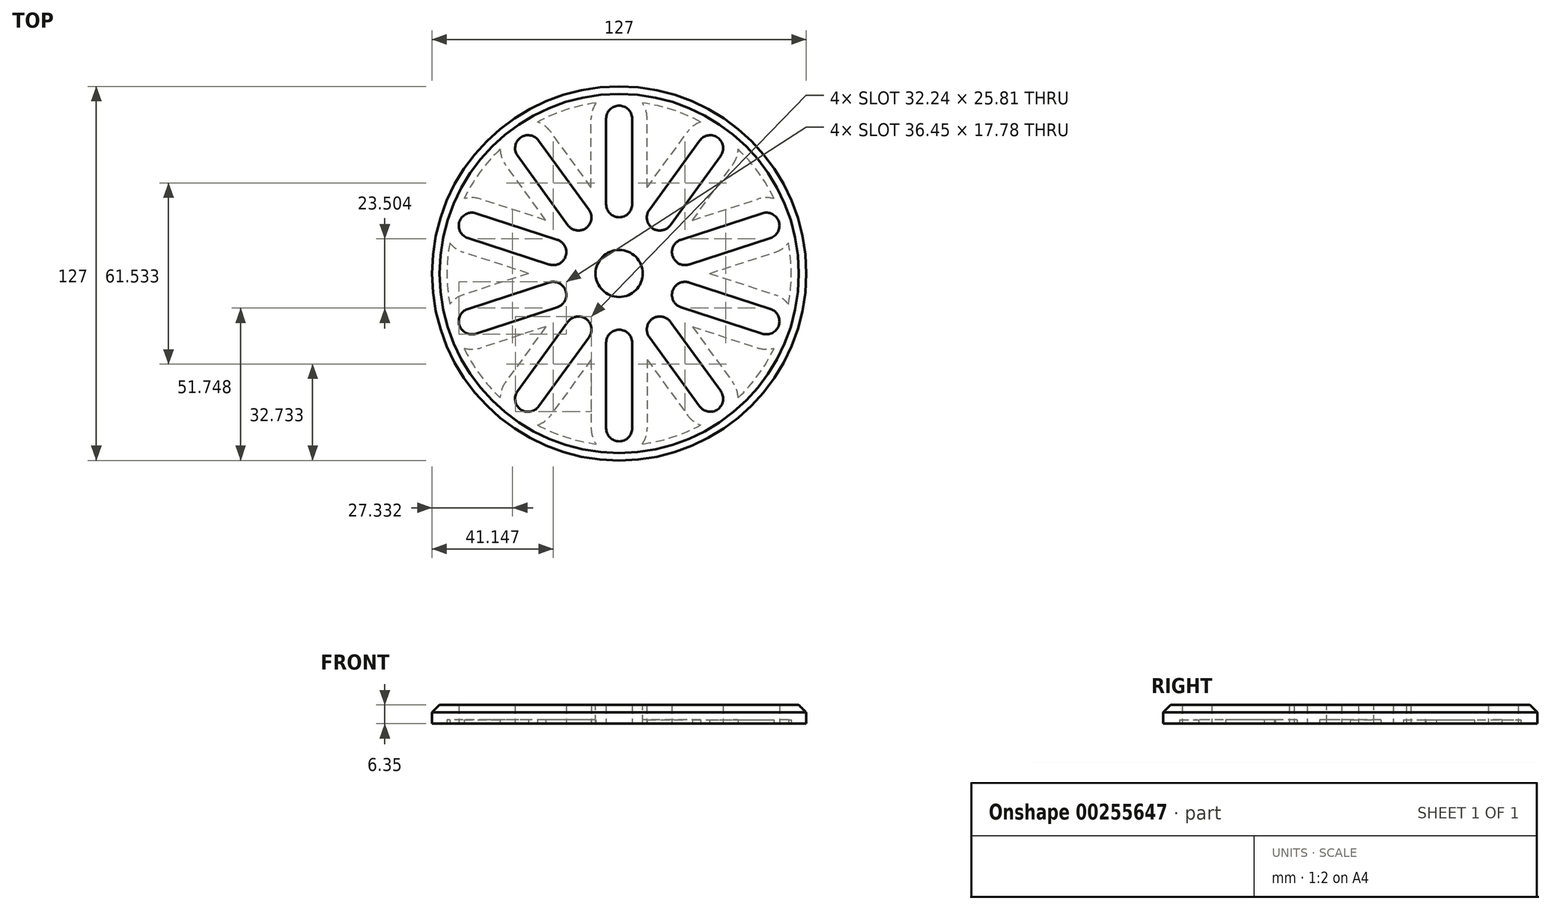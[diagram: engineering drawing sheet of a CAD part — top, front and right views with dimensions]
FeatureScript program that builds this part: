
annotation { "Feature Type Name" : "Feature", "Feature Type Description" : "" }
export const myFeature = defineFeature(function(context is Context, id is Id, definition is map)
    precondition{}
    {
        {
            var Q0;
            Q0=qCreatedBy(makeId("Top.planeOp"),FACE);
            var sketch = newSketch(context, id + "F0", { "sketchPlane" : qUnion([Q0])});
            skCircle(sketch, "E0", {"center": v(0, 0) * mm, "radius": 63.5 * mm});
            skCircle(sketch, "E1", {"center": v(0, 0) * mm, "radius": 12.7 * mm});
            skLineSegment(sketch, "E2.left", {"start": v(4.41, 23.5) * mm, "end": v(4.41, 52.57) * mm});
            skLineSegment(sketch, "E2.right", {"start": v(-4.41, 23.5) * mm, "end": v(-4.41, 52.57) * mm});
            skPoint(sketch, "E2.middle", {"position": v(0, 38.03) * mm});
            skArc(sketch, "E3", {"start": v(-4.41, 23.5) * mm, "mid": v(0, 19.08) * mm, "end": v(4.41, 23.5) * mm});
            skArc(sketch, "E4", {"start": v(4.41, 52.57) * mm, "mid": v(0, 56.98) * mm, "end": v(-4.41, 52.57) * mm});
            skPoint(sketch, "E5.1.0", {"position": v(-22.35, 30.77) * mm});
            skArc(sketch, "E5.1.1", {"start": v(-27.33, 45.12) * mm, "mid": v(-33.5, 46.1) * mm, "end": v(-34.47, 39.94) * mm});
            skArc(sketch, "E5.1.2", {"start": v(-17.38, 16.41) * mm, "mid": v(-11.21, 15.43) * mm, "end": v(-10.24, 21.6) * mm});
            skLineSegment(sketch, "E5.1.3", {"start": v(-17.38, 16.41) * mm, "end": v(-34.47, 39.94) * mm});
            skLineSegment(sketch, "E5.1.4", {"start": v(-10.24, 21.6) * mm, "end": v(-27.33, 45.12) * mm});
            skPoint(sketch, "E5.2.0", {"position": v(-36.17, 11.75) * mm});
            skArc(sketch, "E5.2.1", {"start": v(-48.63, 20.44) * mm, "mid": v(-54.2, 17.6) * mm, "end": v(-51.36, 12.05) * mm});
            skArc(sketch, "E5.2.2", {"start": v(-23.7, 3.06) * mm, "mid": v(-18.14, 5.9) * mm, "end": v(-20.98, 11.46) * mm});
            skLineSegment(sketch, "E5.2.3", {"start": v(-23.7, 3.06) * mm, "end": v(-51.36, 12.05) * mm});
            skLineSegment(sketch, "E5.2.4", {"start": v(-20.98, 11.46) * mm, "end": v(-48.63, 20.44) * mm});
            skPoint(sketch, "E5.3.0", {"position": v(-36.17, -11.75) * mm});
            skArc(sketch, "E5.3.1", {"start": v(-51.36, -12.05) * mm, "mid": v(-54.2, -17.6) * mm, "end": v(-48.63, -20.44) * mm});
            skArc(sketch, "E5.3.2", {"start": v(-20.98, -11.46) * mm, "mid": v(-18.14, -5.9) * mm, "end": v(-23.7, -3.06) * mm});
            skLineSegment(sketch, "E5.3.3", {"start": v(-20.98, -11.46) * mm, "end": v(-48.63, -20.44) * mm});
            skLineSegment(sketch, "E5.3.4", {"start": v(-23.7, -3.06) * mm, "end": v(-51.36, -12.05) * mm});
            skPoint(sketch, "E5.4.0", {"position": v(-22.35, -30.77) * mm});
            skArc(sketch, "E5.4.1", {"start": v(-34.47, -39.94) * mm, "mid": v(-33.5, -46.1) * mm, "end": v(-27.33, -45.12) * mm});
            skArc(sketch, "E5.4.2", {"start": v(-10.24, -21.6) * mm, "mid": v(-11.21, -15.43) * mm, "end": v(-17.38, -16.41) * mm});
            skLineSegment(sketch, "E5.4.3", {"start": v(-10.24, -21.6) * mm, "end": v(-27.33, -45.12) * mm});
            skLineSegment(sketch, "E5.4.4", {"start": v(-17.38, -16.41) * mm, "end": v(-34.47, -39.94) * mm});
            skPoint(sketch, "E5.5.0", {"position": v(0, -38.03) * mm});
            skArc(sketch, "E5.5.1", {"start": v(-4.41, -52.57) * mm, "mid": v(0, -56.98) * mm, "end": v(4.41, -52.57) * mm});
            skArc(sketch, "E5.5.2", {"start": v(4.41, -23.5) * mm, "mid": v(0, -19.08) * mm, "end": v(-4.41, -23.5) * mm});
            skLineSegment(sketch, "E5.5.3", {"start": v(4.41, -23.5) * mm, "end": v(4.41, -52.57) * mm});
            skLineSegment(sketch, "E5.5.4", {"start": v(-4.41, -23.5) * mm, "end": v(-4.41, -52.57) * mm});
            skPoint(sketch, "E5.6.0", {"position": v(22.35, -30.77) * mm});
            skArc(sketch, "E5.6.1", {"start": v(27.33, -45.12) * mm, "mid": v(33.5, -46.1) * mm, "end": v(34.47, -39.94) * mm});
            skArc(sketch, "E5.6.2", {"start": v(17.38, -16.41) * mm, "mid": v(11.21, -15.43) * mm, "end": v(10.24, -21.6) * mm});
            skLineSegment(sketch, "E5.6.3", {"start": v(17.38, -16.41) * mm, "end": v(34.47, -39.94) * mm});
            skLineSegment(sketch, "E5.6.4", {"start": v(10.24, -21.6) * mm, "end": v(27.33, -45.12) * mm});
            skPoint(sketch, "E5.7.0", {"position": v(36.17, -11.75) * mm});
            skArc(sketch, "E5.7.1", {"start": v(48.63, -20.44) * mm, "mid": v(54.2, -17.6) * mm, "end": v(51.36, -12.05) * mm});
            skArc(sketch, "E5.7.2", {"start": v(23.7, -3.06) * mm, "mid": v(18.14, -5.9) * mm, "end": v(20.98, -11.46) * mm});
            skLineSegment(sketch, "E5.7.3", {"start": v(23.7, -3.06) * mm, "end": v(51.36, -12.05) * mm});
            skLineSegment(sketch, "E5.7.4", {"start": v(20.98, -11.46) * mm, "end": v(48.63, -20.44) * mm});
            skPoint(sketch, "E5.8.0", {"position": v(36.17, 11.75) * mm});
            skArc(sketch, "E5.8.1", {"start": v(51.36, 12.05) * mm, "mid": v(54.2, 17.6) * mm, "end": v(48.63, 20.44) * mm});
            skArc(sketch, "E5.8.2", {"start": v(20.98, 11.46) * mm, "mid": v(18.14, 5.9) * mm, "end": v(23.7, 3.06) * mm});
            skLineSegment(sketch, "E5.8.3", {"start": v(20.98, 11.46) * mm, "end": v(48.63, 20.44) * mm});
            skLineSegment(sketch, "E5.8.4", {"start": v(23.7, 3.06) * mm, "end": v(51.36, 12.05) * mm});
            skPoint(sketch, "E5.9.0", {"position": v(22.35, 30.77) * mm});
            skArc(sketch, "E5.9.1", {"start": v(34.47, 39.94) * mm, "mid": v(33.5, 46.1) * mm, "end": v(27.33, 45.12) * mm});
            skArc(sketch, "E5.9.2", {"start": v(10.24, 21.6) * mm, "mid": v(11.21, 15.43) * mm, "end": v(17.38, 16.41) * mm});
            skLineSegment(sketch, "E5.9.3", {"start": v(10.24, 21.6) * mm, "end": v(27.33, 45.12) * mm});
            skLineSegment(sketch, "E5.9.4", {"start": v(17.38, 16.41) * mm, "end": v(34.47, 39.94) * mm});
            skSolve(sketch);
        }
        {
            var Q0;
            Q0=makeQuery(id+"F0.imprint","IMPRINT",FACE,{"disambiguationData":[TD([[makeQuery(id+"F0.imprint","IMPRINT",EDGE,{"derivedFrom":sQuery(id+"F0.wireOp",EDGE,"E0")}),1.0]])]});
            extrude(context, id + "F1", {"entities" : qUnion([Q0]), "depth" : 6.35 * mm});
        }
        {
            var Q0;
            Q0=makeQuery(id+"F1.opExtrude","CAP_FACE",FACE,{"disambiguationData":[OSD([sQuery(id+"F0.wireOp",EDGE,"E0"),sQuery(id+"F0.wireOp",EDGE,"E1"),sQuery(id+"F0.wireOp",EDGE,"E2.left"),sQuery(id+"F0.wireOp",EDGE,"E2.right"),sQuery(id+"F0.wireOp",EDGE,"E3"),sQuery(id+"F0.wireOp",EDGE,"E4"),sQuery(id+"F0.wireOp",EDGE,"E5.1.1"),sQuery(id+"F0.wireOp",EDGE,"E5.1.2"),sQuery(id+"F0.wireOp",EDGE,"E5.1.3"),sQuery(id+"F0.wireOp",EDGE,"E5.1.4"),sQuery(id+"F0.wireOp",EDGE,"E5.2.1"),sQuery(id+"F0.wireOp",EDGE,"E5.2.2"),sQuery(id+"F0.wireOp",EDGE,"E5.2.3"),sQuery(id+"F0.wireOp",EDGE,"E5.2.4"),sQuery(id+"F0.wireOp",EDGE,"E5.3.1"),sQuery(id+"F0.wireOp",EDGE,"E5.3.2"),sQuery(id+"F0.wireOp",EDGE,"E5.3.3"),sQuery(id+"F0.wireOp",EDGE,"E5.3.4"),sQuery(id+"F0.wireOp",EDGE,"E5.4.1"),sQuery(id+"F0.wireOp",EDGE,"E5.4.2"),sQuery(id+"F0.wireOp",EDGE,"E5.4.3"),sQuery(id+"F0.wireOp",EDGE,"E5.4.4"),sQuery(id+"F0.wireOp",EDGE,"E5.5.1"),sQuery(id+"F0.wireOp",EDGE,"E5.5.2"),sQuery(id+"F0.wireOp",EDGE,"E5.5.3"),sQuery(id+"F0.wireOp",EDGE,"E5.5.4"),sQuery(id+"F0.wireOp",EDGE,"E5.6.1"),sQuery(id+"F0.wireOp",EDGE,"E5.6.2"),sQuery(id+"F0.wireOp",EDGE,"E5.6.3"),sQuery(id+"F0.wireOp",EDGE,"E5.6.4"),sQuery(id+"F0.wireOp",EDGE,"E5.7.1"),sQuery(id+"F0.wireOp",EDGE,"E5.7.2"),sQuery(id+"F0.wireOp",EDGE,"E5.7.3"),sQuery(id+"F0.wireOp",EDGE,"E5.7.4"),sQuery(id+"F0.wireOp",EDGE,"E5.8.1"),sQuery(id+"F0.wireOp",EDGE,"E5.8.2"),sQuery(id+"F0.wireOp",EDGE,"E5.8.3"),sQuery(id+"F0.wireOp",EDGE,"E5.8.4"),sQuery(id+"F0.wireOp",EDGE,"E5.9.1"),sQuery(id+"F0.wireOp",EDGE,"E5.9.2"),sQuery(id+"F0.wireOp",EDGE,"E5.9.3"),sQuery(id+"F0.wireOp",EDGE,"E5.9.4")])],"isStart":true});
            shell(context, id + "F2", {"entities" : qUnion([Q0]), "thickness" : 5.08 * mm});
        }
        {
            var Q0;
            Q0=makeQuery(id+"F1.opExtrude","CAP_EDGE",EDGE,{"disambiguationData":[OSD([sQuery(id+"F0.wireOp",EDGE,"E0")])],"isStart":false});
            chamfer(context, id + "F3", {"entities" : qUnion([Q0]), "width" : 2.54 * mm, "tangentPropagation" : true});
        }
        {
            var Q0;
            Q0=makeQuery(id+"F1.opExtrude","CAP_FACE",FACE,{"disambiguationData":[OSD([sQuery(id+"F0.wireOp",EDGE,"E0"),sQuery(id+"F0.wireOp",EDGE,"E1"),sQuery(id+"F0.wireOp",EDGE,"E2.left"),sQuery(id+"F0.wireOp",EDGE,"E2.right"),sQuery(id+"F0.wireOp",EDGE,"E3"),sQuery(id+"F0.wireOp",EDGE,"E4"),sQuery(id+"F0.wireOp",EDGE,"E5.1.1"),sQuery(id+"F0.wireOp",EDGE,"E5.1.2"),sQuery(id+"F0.wireOp",EDGE,"E5.1.3"),sQuery(id+"F0.wireOp",EDGE,"E5.1.4"),sQuery(id+"F0.wireOp",EDGE,"E5.2.1"),sQuery(id+"F0.wireOp",EDGE,"E5.2.2"),sQuery(id+"F0.wireOp",EDGE,"E5.2.3"),sQuery(id+"F0.wireOp",EDGE,"E5.2.4"),sQuery(id+"F0.wireOp",EDGE,"E5.3.1"),sQuery(id+"F0.wireOp",EDGE,"E5.3.2"),sQuery(id+"F0.wireOp",EDGE,"E5.3.3"),sQuery(id+"F0.wireOp",EDGE,"E5.3.4"),sQuery(id+"F0.wireOp",EDGE,"E5.4.1"),sQuery(id+"F0.wireOp",EDGE,"E5.4.2"),sQuery(id+"F0.wireOp",EDGE,"E5.4.3"),sQuery(id+"F0.wireOp",EDGE,"E5.4.4"),sQuery(id+"F0.wireOp",EDGE,"E5.5.1"),sQuery(id+"F0.wireOp",EDGE,"E5.5.2"),sQuery(id+"F0.wireOp",EDGE,"E5.5.3"),sQuery(id+"F0.wireOp",EDGE,"E5.5.4"),sQuery(id+"F0.wireOp",EDGE,"E5.6.1"),sQuery(id+"F0.wireOp",EDGE,"E5.6.2"),sQuery(id+"F0.wireOp",EDGE,"E5.6.3"),sQuery(id+"F0.wireOp",EDGE,"E5.6.4"),sQuery(id+"F0.wireOp",EDGE,"E5.7.1"),sQuery(id+"F0.wireOp",EDGE,"E5.7.2"),sQuery(id+"F0.wireOp",EDGE,"E5.7.3"),sQuery(id+"F0.wireOp",EDGE,"E5.7.4"),sQuery(id+"F0.wireOp",EDGE,"E5.8.1"),sQuery(id+"F0.wireOp",EDGE,"E5.8.2"),sQuery(id+"F0.wireOp",EDGE,"E5.8.3"),sQuery(id+"F0.wireOp",EDGE,"E5.8.4"),sQuery(id+"F0.wireOp",EDGE,"E5.9.1"),sQuery(id+"F0.wireOp",EDGE,"E5.9.2"),sQuery(id+"F0.wireOp",EDGE,"E5.9.3"),sQuery(id+"F0.wireOp",EDGE,"E5.9.4")])],"isStart":false});
            var sketch = newSketch(context, id + "F4", { "sketchPlane" : qUnion([Q0])});
            skCircle(sketch, "E6", {"center": v(0, 0) * mm, "radius": 15.56 * mm});
            skCircle(sketch, "E7", {"center": v(0, 0) * mm, "radius": 8 * mm});
            skSolve(sketch);
        }
        {
            var Q0;
            Q0=makeQuery(id+"F4.imprint","IMPRINT",FACE,{"disambiguationData":[TD([[makeQuery(id+"F4.imprint","IMPRINT",EDGE,{"derivedFrom":sQuery(id+"F4.wireOp",EDGE,"E7")}),-1.0]])]});
            extrude(context, id + "F5", {"entities" : qUnion([Q0]), "operationType" : NewBodyOperationType.ADD, "oppositeDirection" : true, "depth" : 6.35 * mm});
        }
    });
